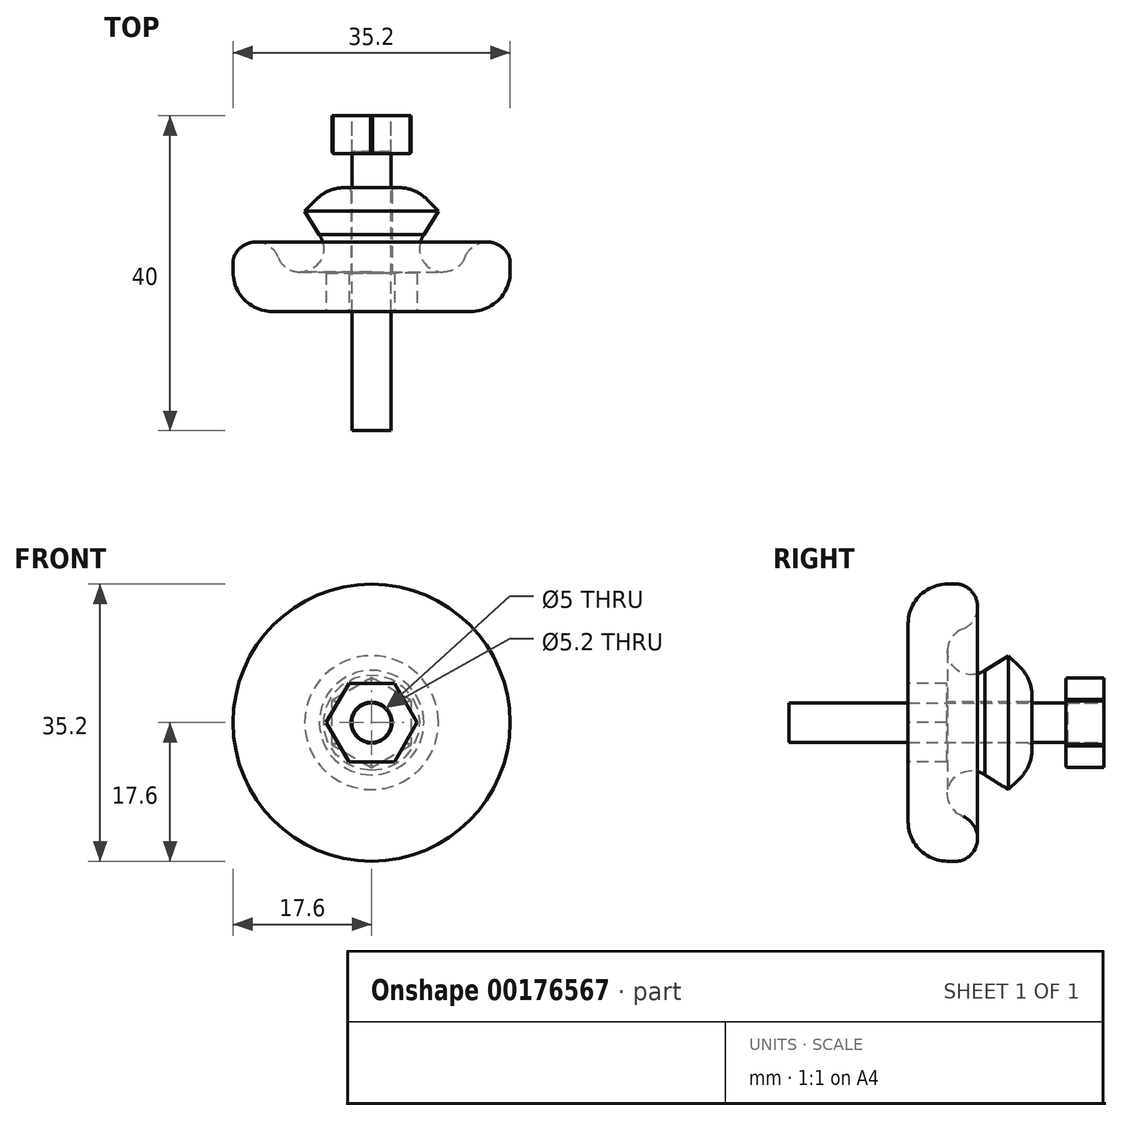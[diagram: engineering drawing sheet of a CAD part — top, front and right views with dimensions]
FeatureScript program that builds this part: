
annotation { "Feature Type Name" : "Feature", "Feature Type Description" : "" }
export const myFeature = defineFeature(function(context is Context, id is Id, definition is map)
    precondition{}
    {
        {
            var Q0;
            Q0=qCreatedBy(makeId("Front.planeOp"),FACE);
            var sketch = newSketch(context, id + "F0", { "sketchPlane" : qUnion([Q0])});
            skCircle(sketch, "E0.cCircle", {"center": v(0, 0) * mm, "radius": 5 * mm, "construction": true});
            skLineSegment(sketch, "E0.0", {"start": v(5, 2.89) * mm, "end": v(5, -2.89) * mm});
            skLineSegment(sketch, "E0.1", {"start": v(5, -2.89) * mm, "end": v(0, -5.77) * mm});
            skLineSegment(sketch, "E0.2", {"start": v(0, -5.77) * mm, "end": v(-5, -2.89) * mm});
            skLineSegment(sketch, "E0.3", {"start": v(-5, -2.89) * mm, "end": v(-5, 2.89) * mm});
            skLineSegment(sketch, "E0.4", {"start": v(-5, 2.89) * mm, "end": v(0, 5.77) * mm});
            skLineSegment(sketch, "E0.5", {"start": v(0, 5.77) * mm, "end": v(5, 2.89) * mm});
            skPoint(sketch, "E0.0.midPoint", {"position": v(5, 0) * mm});
            skCircle(sketch, "E1", {"center": v(0, 0) * mm, "radius": 2.5 * mm});
            skSolve(sketch);
        }
        {
            var Q0;
            Q0=makeQuery(id+"F0.imprint","IMPRINT",FACE,{"disambiguationData":[TD([[makeQuery(id+"F0.imprint","IMPRINT",EDGE,{"derivedFrom":sQuery(id+"F0.wireOp",EDGE,"E0.0")}),-1.0]])]});
            extrude(context, id + "F1", {"entities" : qUnion([Q0]), "depth" : 4.8 * mm});
        }
        {
            var Q0;
            Q0=makeQuery(id+"F1.opExtrude","CAP_EDGE",EDGE,{"disambiguationData":[OSD([sQuery(id+"F0.wireOp",EDGE,"E1")])],"isStart":false});
            var Q1;
            Q1=makeQuery(id+"F1.opExtrude","SWEPT_EDGE",EDGE,{"disambiguationData":[OSD([sQuery(id+"F0.wireOp",EDGE,"E0.0"),sQuery(id+"F0.wireOp",EDGE,"E0.5")])]});
            var Q2;
            Q2=makeQuery(id+"F1.opExtrude","SWEPT_EDGE",EDGE,{"disambiguationData":[OSD([sQuery(id+"F0.wireOp",EDGE,"E0.0"),sQuery(id+"F0.wireOp",EDGE,"E0.1")])]});
            var Q3;
            Q3=makeQuery(id+"F1.opExtrude","SWEPT_EDGE",EDGE,{"disambiguationData":[OSD([sQuery(id+"F0.wireOp",EDGE,"E0.1"),sQuery(id+"F0.wireOp",EDGE,"E0.2")])]});
            var Q4;
            Q4=makeQuery(id+"F1.opExtrude","SWEPT_EDGE",EDGE,{"disambiguationData":[OSD([sQuery(id+"F0.wireOp",EDGE,"E0.2"),sQuery(id+"F0.wireOp",EDGE,"E0.3")])]});
            var Q5;
            Q5=makeQuery(id+"F1.opExtrude","SWEPT_EDGE",EDGE,{"disambiguationData":[OSD([sQuery(id+"F0.wireOp",EDGE,"E0.4"),sQuery(id+"F0.wireOp",EDGE,"E0.5")])]});
            var Q6;
            Q6=makeQuery(id+"F1.opExtrude","SWEPT_EDGE",EDGE,{"disambiguationData":[OSD([sQuery(id+"F0.wireOp",EDGE,"E0.3"),sQuery(id+"F0.wireOp",EDGE,"E0.4")])]});
            chamfer(context, id + "F2", {"entities" : qUnion([Q0, Q1, Q2, Q3, Q4, Q5, Q6]), "width" : 0.25 * mm, "tangentPropagation" : true});
        }
        {
            var Q0;
            Q0=makeQuery(id+"F1.opExtrude","CAP_FACE",FACE,{"disambiguationData":[OSD([sQuery(id+"F0.wireOp",EDGE,"E0.0"),sQuery(id+"F0.wireOp",EDGE,"E0.1"),sQuery(id+"F0.wireOp",EDGE,"E0.2"),sQuery(id+"F0.wireOp",EDGE,"E0.3"),sQuery(id+"F0.wireOp",EDGE,"E0.4"),sQuery(id+"F0.wireOp",EDGE,"E0.5"),sQuery(id+"F0.wireOp",EDGE,"E1")])],"isStart":false});
            fillet(context, id + "F3", {"entities" : qUnion([Q0]), "radius" : 0.5 * mm, "tangentPropagation" : true, "rho" : 0.8, "crossSection" : FilletCrossSection.CONIC, "allowEdgeOverflow" : false});
        }
        {
            var Q0;
            Q0=qCreatedBy(makeId("Front.planeOp"),FACE);
            var sketch = newSketch(context, id + "F4", { "sketchPlane" : qUnion([Q0])});
            skCircle(sketch, "E2", {"center": v(0, 0) * mm, "radius": 2.5 * mm});
            skSolve(sketch);
        }
        {
            var Q0;
            Q0 = qSketchRegion(id + "F4", true);
            extrude(context, id + "F5", {"entities" : qUnion([Q0]), "depth" : 40 * mm});
        }
        {
            var Q0;
            Q0=qCreatedBy(makeId("Top.planeOp"),FACE);
            var sketch = newSketch(context, id + "F6", { "sketchPlane" : qUnion([Q0])});
            skArc(sketch, "E3", {"start": v(6.64, -15.12) * mm, "mid": v(7.66, -19.5) * mm, "end": v(11.88, -17.95) * mm});
            skLineSegment(sketch, "E4", {"start": v(2.6, -24.86) * mm, "end": v(12.6, -24.86) * mm});
            skLineSegment(sketch, "E5", {"start": v(17.6, -19.86) * mm, "end": v(17.6, -18.65) * mm});
            skLineSegment(sketch, "E6", {"start": v(18.36, -16.04) * mm, "end": v(18.32, -16.04) * mm});
            skArc(sketch, "E7.filletArc", {"start": v(17.44, -17.86) * mm, "mid": v(14.63, -16.04) * mm, "end": v(11.88, -17.95) * mm});
            skArc(sketch, "E8.filletArc", {"start": v(17.6, -18.65) * mm, "mid": v(17.56, -18.25) * mm, "end": v(17.44, -17.86) * mm});
            skPoint(sketch, "E9.visualSharp", {"position": v(17.6, -24.86) * mm});
            skArc(sketch, "E9.filletArc", {"start": v(12.6, -24.86) * mm, "mid": v(16.14, -23.4) * mm, "end": v(17.6, -19.86) * mm});
            skLineSegment(sketch, "E10", {"start": v(0, -26.8) * mm, "end": v(0, -10.28) * mm, "construction": true});
            skLineSegment(sketch, "E11", {"start": v(3.48, -9.14) * mm, "end": v(2.6, -9.14) * mm});
            skLineSegment(sketch, "E12", {"start": v(2.6, -24.86) * mm, "end": v(2.6, -9.14) * mm});
            skLineSegment(sketch, "E13", {"start": v(8.5, -12.14) * mm, "end": v(6.64, -15.12) * mm});
            skLineSegment(sketch, "E14", {"start": v(8.5, -12.14) * mm, "end": v(7.07, -10.67) * mm});
            skPoint(sketch, "E15.visualSharp", {"position": v(5.6, -9.14) * mm});
            skArc(sketch, "E15.filletArc", {"start": v(7.07, -10.67) * mm, "mid": v(5.43, -9.54) * mm, "end": v(3.48, -9.14) * mm});
            skSolve(sketch);
        }
        {
            var Q0;
            Q0=makeQuery(id+"F6.imprint","IMPRINT",FACE,{"disambiguationData":[TD([[makeQuery(id+"F6.imprint","IMPRINT",EDGE,{"derivedFrom":sQuery(id+"F6.wireOp",EDGE,"E3")}),-1.0]])]});
            var Q1;
            Q1=sQuery(id+"F6.wireOp",EDGE,"E10");
            revolve(context, id + "F7", {"entities" : qUnion([Q0]), "axis" : qUnion([Q1]), "revolveType" : RevolveType.FULL});
        }
        {
            var Q0;
            Q0=makeQuery(id+"F7.opRevolve","SWEPT_FACE",FACE,{"disambiguationData":[OSD([sQuery(id+"F6.wireOp",EDGE,"E4")])]});
            var sketch = newSketch(context, id + "F8", { "sketchPlane" : qUnion([Q0])});
            skCircle(sketch, "E16.cCircle", {"center": v(0, 0) * mm, "radius": 5 * mm, "construction": true});
            skLineSegment(sketch, "E16.0", {"start": v(-2.89, 5) * mm, "end": v(2.89, 5) * mm});
            skLineSegment(sketch, "E16.1", {"start": v(2.89, 5) * mm, "end": v(5.77, 0) * mm});
            skLineSegment(sketch, "E16.2", {"start": v(5.77, 0) * mm, "end": v(2.89, -5) * mm});
            skLineSegment(sketch, "E16.3", {"start": v(2.89, -5) * mm, "end": v(-2.89, -5) * mm});
            skLineSegment(sketch, "E16.4", {"start": v(-2.89, -5) * mm, "end": v(-5.77, 0) * mm});
            skLineSegment(sketch, "E16.5", {"start": v(-5.77, 0) * mm, "end": v(-2.89, 5) * mm});
            skPoint(sketch, "E16.0.midPoint", {"position": v(0, 5) * mm});
            skCircle(sketch, "E17", {"center": v(0, 0) * mm, "radius": 2.55 * mm});
            skSolve(sketch);
        }
        {
            var Q0;
            Q0 = qSketchRegion(id + "F8", true);
            extrude(context, id + "F9", {"entities" : qUnion([Q0]), "operationType" : NewBodyOperationType.REMOVE, "oppositeDirection" : true, "depth" : 4.9 * mm});
        }
        {
            var Q0;
            Q0=makeQuery(id+"F7.opRevolve","SWEPT_EDGE",EDGE,{"disambiguationData":[OSD([sQuery(id+"F6.wireOp",EDGE,"7gwzJt1p-tAbm-67kc-ErE0-QECYMBSrYc4t"),sQuery(id+"F6.wireOp",EDGE,"E11")])]});
            fillet(context, id + "F10", {"entities" : qUnion([Q0]), "radius" : .5 * mm, "tangentPropagation" : true, "allowEdgeOverflow" : false});
        }
    });
